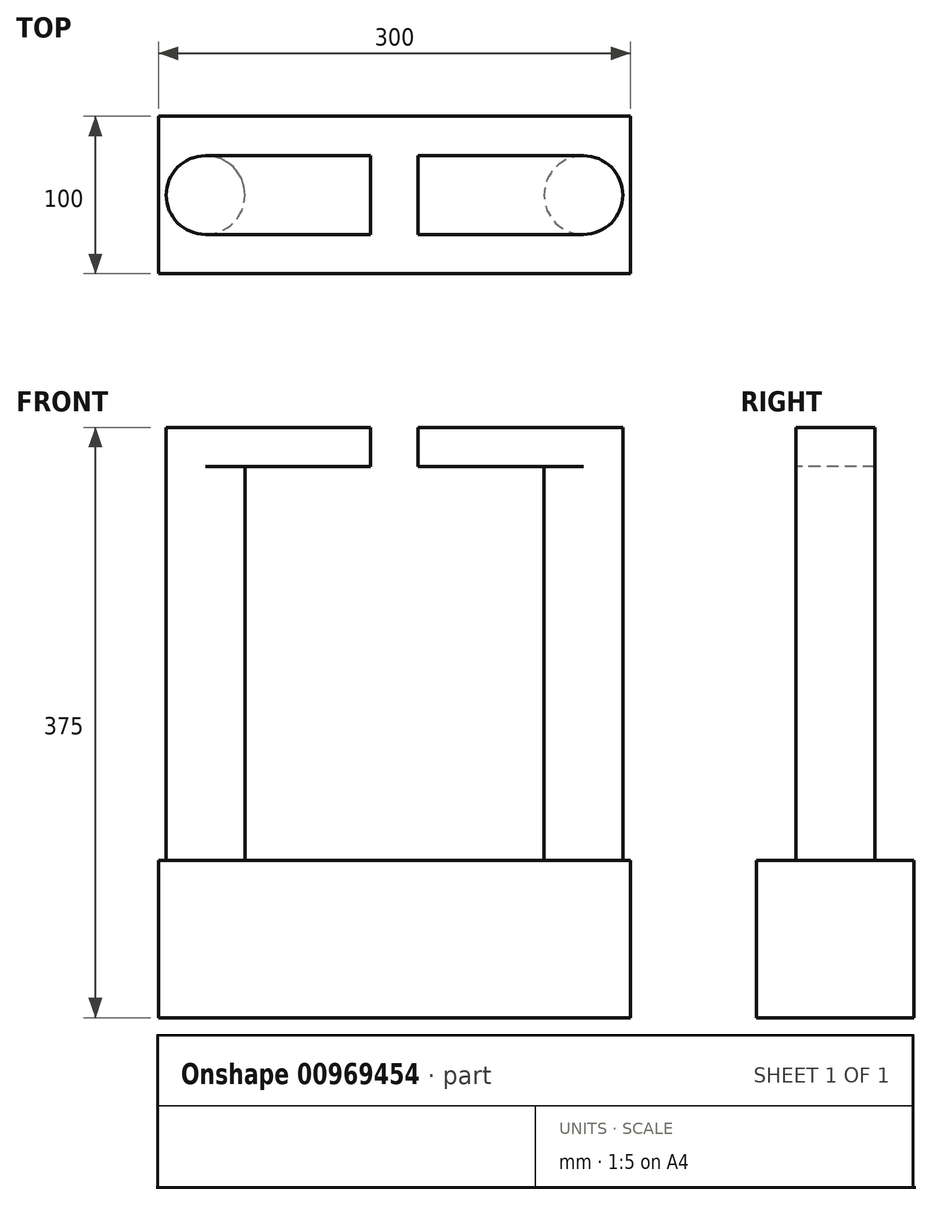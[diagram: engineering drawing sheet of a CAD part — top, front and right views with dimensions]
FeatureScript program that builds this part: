
annotation { "Feature Type Name" : "Feature", "Feature Type Description" : "" }
export const myFeature = defineFeature(function(context is Context, id is Id, definition is map)
    precondition{}
    {
        {
            var Q0;
            Q0=qCreatedBy(makeId("Top.planeOp"),FACE);
            var sketch = newSketch(context, id + "F0", { "sketchPlane" : qUnion([Q0])});
            skLineSegment(sketch, "E0.bottom", {"start": v(150, -50) * mm, "end": v(-150, -50) * mm});
            skLineSegment(sketch, "E0.top", {"start": v(150, 50) * mm, "end": v(-150, 50) * mm});
            skLineSegment(sketch, "E0.left", {"start": v(150, -50) * mm, "end": v(150, 50) * mm});
            skLineSegment(sketch, "E0.right", {"start": v(-150, -50) * mm, "end": v(-150, 50) * mm});
            skPoint(sketch, "E0.middle", {"position": v(0, 0) * mm});
            skSolve(sketch);
        }
        {
            var Q0;
            Q0 = qSketchRegion(id + "F0", true);
            extrude(context, id + "F1", {"entities" : qUnion([Q0]), "depth" : 100 * mm, "offsetDistance" : 25 * mm});
        }
        {
            var Q0;
            Q0=makeQuery(id+"F1.opExtrude","CAP_FACE",FACE,{"disambiguationData":[OSD([sQuery(id+"F0.wireOp",EDGE,"E0.bottom"),sQuery(id+"F0.wireOp",EDGE,"E0.top"),sQuery(id+"F0.wireOp",EDGE,"E0.left"),sQuery(id+"F0.wireOp",EDGE,"E0.right")])],"isStart":false});
            var sketch = newSketch(context, id + "F2", { "sketchPlane" : qUnion([Q0])});
            skLineSegment(sketch, "E1", {"start": v(0, 50) * mm, "end": v(0, -50) * mm, "construction": true});
            skSolve(sketch);
        }
        {
            var Q0;
            Q0=makeQuery(id+"F2.imprint","IMPRINT",FACE,{"disambiguationData":[TD([[makeQuery(id+"F2.imprint","IMPRINT",EDGE,{"derivedFrom":makeQuery(id+"F1.opExtrude","CAP_EDGE",EDGE,{"disambiguationData":[OSD([sQuery(id+"F0.wireOp",EDGE,"E0.bottom")])],"isStart":false})}),-1.0]])]});
            var sketch = newSketch(context, id + "F3", { "sketchPlane" : qUnion([Q0])});
            skCircle(sketch, "E2", {"center": v(120, 0) * mm, "radius": 25 * mm});
            skCircle(sketch, "E3.MirrorC", {"center": v(-120, 0) * mm, "radius": 25 * mm});
            skSolve(sketch);
        }
        {
            var Q0;
            Q0 = qSketchRegion(id + "F3", true);
            extrude(context, id + "F4", {"entities" : qUnion([Q0]), "operationType" : NewBodyOperationType.ADD, "depth" : 250 * mm, "offsetDistance" : 25 * mm});
        }
        {
            var Q0;
            Q0=makeQuery(id+"F4.opExtrude","CAP_FACE",FACE,{"disambiguationData":[OSD([sQuery(id+"F3.wireOp",EDGE,"E3.MirrorC")])],"isStart":false});
            var sketch = newSketch(context, id + "F5", { "sketchPlane" : qUnion([Q0])});
            skLineSegment(sketch, "E4.bottom", {"start": v(-120, 25) * mm, "end": v(120, 25) * mm});
            skLineSegment(sketch, "E4.top", {"start": v(-120, -25) * mm, "end": v(120, -25) * mm});
            skLineSegment(sketch, "E4.left", {"start": v(-120, 25) * mm, "end": v(-120, -25) * mm});
            skLineSegment(sketch, "E4.right", {"start": v(120, 25) * mm, "end": v(120, -25) * mm});
            skSolve(sketch);
        }
        {
            var Q0;
            {var subQ0=sQuery(id+"F5.wireOp",EDGE,"E4.bottom");Q0=makeQuery(id+"F5.imprint","IMPRINT",FACE,{"disambiguationData":[TD([[makeQuery(id+"F5.imprint","IMPRINT",EDGE,{"derivedFrom":subQ0}),-1.0]])]});}
            var Q1;
            {var subQ0=sQuery(id+"F5.wireOp",EDGE,"E4.left");Q1=makeQuery(id+"F5.imprint","IMPRINT",FACE,{"disambiguationData":[TD([[makeQuery(id+"F5.imprint","IMPRINT",EDGE,{"derivedFrom":subQ0}),1.0]])]});}
            extrude(context, id + "F6", {"entities" : qUnion([Q0, Q1]), "operationType" : NewBodyOperationType.ADD, "depth" : 25 * mm, "offsetDistance" : 25 * mm});
        }
        {
            var Q0;
            Q0=makeQuery(id+"F4.opExtrude","CAP_FACE",FACE,{"disambiguationData":[OSD([sQuery(id+"F3.wireOp",EDGE,"E3.MirrorC")])],"isStart":false});
            var Q1;
            Q1=makeQuery(id+"F4.opExtrude","CAP_FACE",FACE,{"disambiguationData":[OSD([sQuery(id+"F3.wireOp",EDGE,"E2")])],"isStart":false});
            var Q2;
            Q2=makeQuery(id+"F6.opExtrude","CAP_FACE",FACE,{"disambiguationData":[OSD([sQuery(id+"F5.wireOp",EDGE,"E4.bottom"),sQuery(id+"F5.wireOp",EDGE,"E4.top"),sQuery(id+"F5.wireOp",EDGE,"E4.left"),sQuery(id+"F5.wireOp",EDGE,"E4.right")])],"isStart":false});
            extrude(context, id + "F7", {"entities" : qUnion([Q0, Q1]), "operationType" : NewBodyOperationType.ADD, "endBound" : BoundingType.UP_TO_SURFACE, "depth" : 25 * mm, "endBoundEntityFace" : qUnion([Q2]), "offsetDistance" : 25 * mm});
        }
        {
            var Q0;
            Q0=makeQuery(id+"F6.opExtrude","SWEPT_FACE",FACE,{"disambiguationData":[OSD([sQuery(id+"F5.wireOp",EDGE,"E4.top")])]});
            var sketch = newSketch(context, id + "F8", { "sketchPlane" : qUnion([Q0])});
            skLineSegment(sketch, "E5.bottom", {"start": v(15.1, 375) * mm, "end": v(-15.1, 375) * mm});
            skLineSegment(sketch, "E5.top", {"start": v(15.1, 325) * mm, "end": v(-15.1, 325) * mm});
            skLineSegment(sketch, "E5.left", {"start": v(15.1, 375) * mm, "end": v(15.1, 325) * mm});
            skLineSegment(sketch, "E5.right", {"start": v(-15.1, 375) * mm, "end": v(-15.1, 325) * mm});
            skPoint(sketch, "E5.middle", {"position": v(0, 350) * mm});
            skSolve(sketch);
        }
        {
            var Q0;
            {var subQ0=sQuery(id+"F8.wireOp",EDGE,"E5.bottom");Q0=makeQuery(id+"F8.imprint","IMPRINT",FACE,{"disambiguationData":[TD([[makeQuery(id+"F8.imprint","IMPRINT",EDGE,{"derivedFrom":subQ0}),-1.0]])]});}
            extrude(context, id + "F9", {"entities" : qUnion([Q0]), "operationType" : NewBodyOperationType.REMOVE, "endBound" : BoundingType.THROUGH_ALL, "oppositeDirection" : true, "depth" : 25 * mm, "offsetDistance" : 25 * mm});
        }
    });
